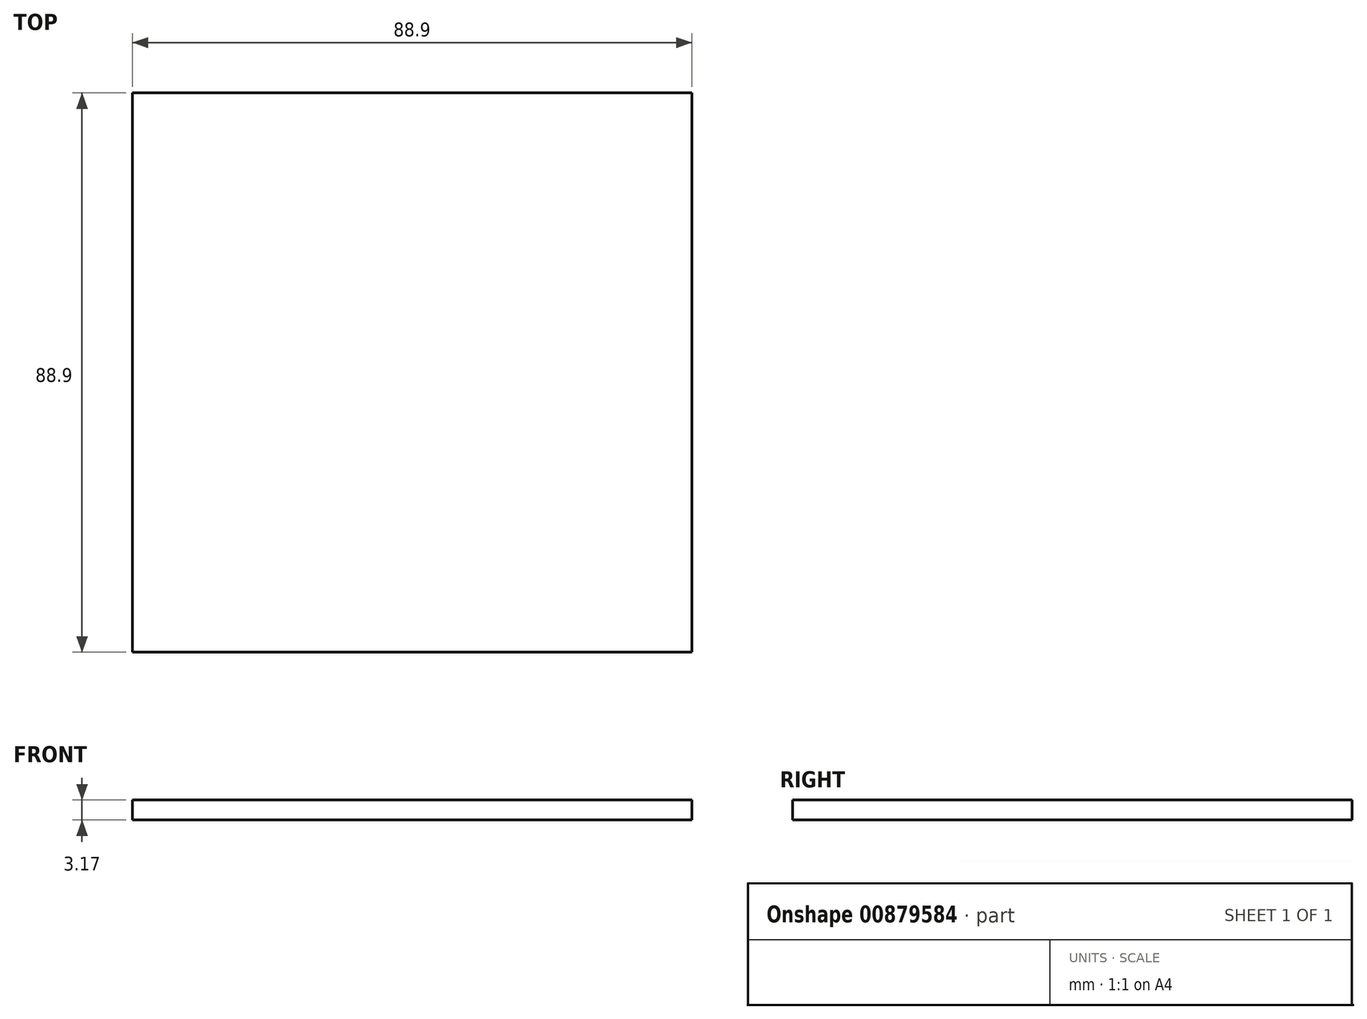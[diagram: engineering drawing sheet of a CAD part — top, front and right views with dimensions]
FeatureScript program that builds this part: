
annotation { "Feature Type Name" : "Feature", "Feature Type Description" : "" }
export const myFeature = defineFeature(function(context is Context, id is Id, definition is map)
    precondition{}
    {
        {
            var Q0;
            Q0=qCreatedBy(makeId("Top.planeOp"),FACE);
            var sketch = newSketch(context, id + "F0", { "sketchPlane" : qUnion([Q0])});
            skLineSegment(sketch, "E0.bottom", {"start": v(44.45, -44.45) * mm, "end": v(-44.45, -44.45) * mm});
            skLineSegment(sketch, "E0.top", {"start": v(44.45, 44.45) * mm, "end": v(-44.45, 44.45) * mm});
            skLineSegment(sketch, "E0.left", {"start": v(44.45, -44.45) * mm, "end": v(44.45, 44.45) * mm});
            skLineSegment(sketch, "E0.right", {"start": v(-44.45, -44.45) * mm, "end": v(-44.45, 44.45) * mm});
            skPoint(sketch, "E0.middle", {"position": v(0, 0) * mm});
            skSolve(sketch);
        }
        {
            var Q0;
            Q0=makeQuery(id+"F0.imprint","IMPRINT",FACE,{"disambiguationData":[TD([[makeQuery(id+"F0.imprint","IMPRINT",EDGE,{"derivedFrom":sQuery(id+"F0.wireOp",EDGE,"E0.bottom")}),-1.0]])]});
            extrude(context, id + "F1", {"entities" : qUnion([Q0]), "depth" : 3.17 * mm, "offsetDistance" : 25.4 * mm});
        }
    });
